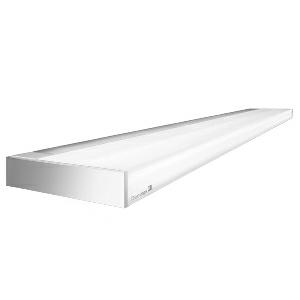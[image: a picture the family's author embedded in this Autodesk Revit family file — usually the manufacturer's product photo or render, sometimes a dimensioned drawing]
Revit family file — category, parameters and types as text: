
# Revit family: vanera_bed_-_vaw_8000_830_d_00812230_1939
name_source: partatom
category: Lighting Fixtures
units: mm (PartAtom-declared; Revit-internal decimal feet)

## family parameters
Cut with Voids When Loaded = No
Host = Face
Light Source = No
Part Type = Normal
Room Calculation Point = No
Round Connector Dimension = Use Diameter
Shared = No

## types (1)
- AL+LL (1 x LED, 7500 lm, 3000K)
    Apparent Load = 71 VA
    Approval mark = CE
    CIE Flux Codes = 46 76 94 28 100
    Color Rendering = 80-89
    Color Temperature = 3000K
    Control Gear = Electronic ballast
    Default Elevation = 2000 mm  [stored 6.56168 ft]
    Description = VAW 8000/830/D|Wall-mounted luminaire|light source:   Warm white   |work equipment: Power supply unit|luminous flux: 7500 lm|light distribution: Direct/indirect|class of protection: I|technology: Two-stage switchable|mains lead: Connection box 3 pin|glare control: Diffusor|special features: General light and night light DALI, General light, indirect, 3000K, Ra80, DALI Load 2x, DIN EN 60598-2-25, Reading light, direct, 3,00K, Ra80|
    Frequency = 50 Hz, 60 Hz
    Height = 45 mm
    Lamp = 1 x LED
    Lamp Light Flux = 7500 lm
    Lamp count = 1
    Length = 1200 mm
    Luminous efficacy = 106 lm/W
    Manufacturer = Waldmann
    ModVariant = No
    Model = 00812230
    Mounting Place = Wall
    Mounting Type = Surface mounted
    Number of Poles = 1
    OnlyDefault = Yes
    Power Factor = 1
    Product Name = VANERA.bed - VAW 8000/830/D
    Product group = Wall mounted Luminaire
    ProductGroupID = 20
    Protection Class = Protection class I
    Protection Degree = Degree of protection
    RLX_Detail_Level = 1
    RLX_Emergency_Light_Flux = 0 lm
    RLX_Emergency_Type = 0
    RLX_Emergency_Type_DB = No
    RlxData = <blob elided: 63217 chars, md5=2c362f33>
    Socket = socket
    Standby Power = 0 W
    System Light Flux = 7500 lm
    System Power = 71 W
    Type Comments = Allgemeinlicht und Leselicht
    Type Image = vanera_opal_54_54_w.jpg
    URL = http://relux.com
    VarID = al_ll_67c3
    Voltage = 230 V
    Voltage Range = 220-240 V
    Weight = 0.00 kg
    Width = 160 mm

note: [stored X ft] marks values corroborated as IEEE doubles in the binary element streams (Revit-internal decimal feet)

## geometry (parser evidence)
native form markers: Blend x4, Sweep x15
no freeform markers — native parametric forms only
